# Revit family: Grohe_PlumbingFixture_Essentials_ToiletRollHolder_40367001a
name_source: partatom
category: Plumbing Fixtures
revit_build: Autodesk Revit 2018 (Build: 20190510_1515(x64)
units: mm (PartAtom-declared; Revit-internal decimal feet)

## family parameters
Cut with Voids When Loaded = No
Host = Face
OmniClass Number = 23.65.00.00
OmniClass Title = Supply and Distribution of Liquids and Gases
Part Type = Normal
Room Calculation Point = No
Round Connector Dimension = Use Diameter
Shared = No

## types (1)
- 40367001
    ADACompliant = No
    Assembly Code = D2010
    AssetType = Fixed
    BIMObjectName = Grohe_PlumbingFixture_Essentials_ToiletRollHolder_40367001
    CWFU = 0
    ClassificationName = Uniclass 2015
    ClassificationValue = Pr_40_20_76_88
    ColdWaterConnectionDiameter = 10 mm  [stored 0.0328084 ft]
    Color = Chrome
    Cost = 0 $
    Default Elevation = 0 mm  [stored 0 ft]
    Description = Luxurious bathrooms are all about harmony. So add a selection of our complementary GROHE Essentials accessories such as the toilet paper holder with cover. It has a durable, easy-care GROHE StarLight chrome finish that will sparkle for years and is super easy to fit – just follow the clear step-by-step instructions. Don’t forget to check out other products in the comprehensive collection such as the robe hook, toilet brush set and numerous towel rails and bath grips. Or for added ease and convenience, why not try one of our all-in-one sets? GROHE Essentials accessories – precision craftsmanship, highest quality materials and design that lasts. The perfect finishing touch for bathrooms of all shapes and sizes!
    DocumentationCertificates = www.grohe.co.uk/
    DocumentationInstallationGuide = www.grohe.co.uk/
    DocumentationLiterature = www.grohe.co.uk/
    DocumentationMaintenance = www.grohe.co.uk/
    DocumentationTechnical = www.grohe.co.uk/
    DurationUnit = Years
    Ecojoy = No
    ExpectedLife = 0
    FaucetMaterial = Grohe-Chrome
    Features = material: metal 
with cover 
concealed fastening 
GROHE StarLight chrome finish 
suitable for screwing (including screws and dowels) or gluing (glue 40 915 000 sold separately)
    HWFU = 0
    HotWaterConnectionDiameter = 10 mm  [stored 0.0328084 ft]
    IfcExportAs = IfcPipeFitting
    IfcExportType = IfcPipeFittingType
    Keynote = N13
    LowEmittingMaterial = No
    Manufacturer = Grohe
    ManufacturerName = Grohe
    MasterformatNumber = 01 52 19
    MasterformatTitle = Sanitary Facilities
    Model = ESSENTIALS
    ModelNumber = 40367001
    ModelReference = ESSENTIALS - TOILET ROLL HOLDER
    NBSDescription = Toilet roll holders
    NBSObjectName = Grohe - Toilet roll holders
    NBSReference = 45-35-72/368
    NominalDepth = 0 mm  [stored 0 ft]
    NominalHeight = 0 mm  [stored 0 ft]
    NominalLength = 0 mm  [stored 0 ft]
    ProductPageURL = https://www.grohe.co.uk
    ProductionYear = 2020
    Type Comments = TOILET ROLL HOLDER
    TypeName = ESSENTIALS - TOILET ROLL HOLDER
    URL = www.grohe.com
    WarrantyDurationLabor = 0
    WarrantyDurationParts = 0
    WarrantyDurationUnit = Years
    _BSBibleVersion = 16
    _BimSpecGuid = 0
    _CurrentRevision = 1
    _DistributedBy = www.bimstore.co
    _ObjectUserGuide = www.bimstore.co

note: [stored X ft] marks values corroborated as IEEE doubles in the binary element streams (Revit-internal decimal feet)

## geometry (parser evidence)
native form markers: Sweep x3
no freeform markers — native parametric forms only
